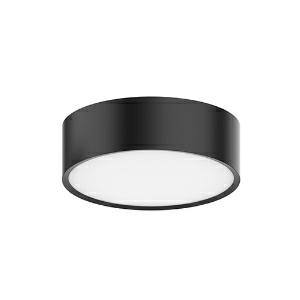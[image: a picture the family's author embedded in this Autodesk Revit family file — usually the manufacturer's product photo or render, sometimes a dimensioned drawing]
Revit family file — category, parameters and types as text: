
# Revit family: ledceilinglu-e_rd112-14w-840-bl_540001295800
name_source: partatom
category: Leuchten
revit_build: Autodesk Revit 2016 (Build: 20190508_0715(x64)
units: mm (PartAtom-declared; Revit-internal decimal feet)

## family parameters
Basisbauteil = Fläche
Beim Laden mit Abzugskörper schneiden = Nein
Bemaßung runder Anschluss = Durchmesser verwenden
Gemeinsam genutzt = Nein
Lichtquelle = Nein
Raumberechnungspunkt = Nein
Teiletyp = Normal

## types (1)
- LEDCeilingLu-E Rd112-14W-840-BL (1 x LED, 1260 lm)
    Approval mark = CE
    Beschreibung = Stylish and compact ceiling luminaire. Clean “twist-and-lock” mounting system. High quality full metal body. Low height of only 46mm. Suitable for ceiling and wall mounting.
    CIE Flux Codes = 50 80 96 100 100
    Control Gear = Electronic ballast
    Height = 100 mm  [stored 0.328084 ft]
    Hersteller = OPPLE
    Lamp Light Flux = 1260 lm
    Lamp count = 1
    Lampe = 1 x LED
    Length = 100 mm  [stored 0.328084 ft]
    Luminous efficacy = 90 lm/W
    ModVariant = Nein
    Modell = 540001295800
    Mounting Place = Wall, Ceiling
    Mounting Type = Surface mounted
    Number of Poles = 1
    OnlyDefault = Ja
    Power Factor = 1
    Product Name = LEDCeilingLu-E Rd112-14W-840-BL
    Product group = Ceiling Light Luna
    ProductGroupID = 305
    Protection Class = Protection class II
    Protection Degree = IP 20
    RLX_Detail_Level = 1
    RlxData = <blob elided: 125997 chars, md5=75ec70f6>
    Scheinlast = 14 VA
    Socket = socket
    Standby Power = 0 W
    System Light Flux = 1260 lm
    System Power = 14 W
    Typenbild = luna_bl_rd112.jpg
    Typenkommentare = Product without accessories
    URL = http://relux.com
    VarID = ---
    Voltage = 230 V
    Voltage Range = 220-240 V
    Vorgabe-Ansicht = 1800 mm
    Weight = 0.00 kg
    Width = 100 mm  [stored 0.328084 ft]

note: [stored X ft] marks values corroborated as IEEE doubles in the binary element streams (Revit-internal decimal feet)

## geometry (parser evidence)
native form markers: Blend x4, Sweep x11
no freeform markers — native parametric forms only
